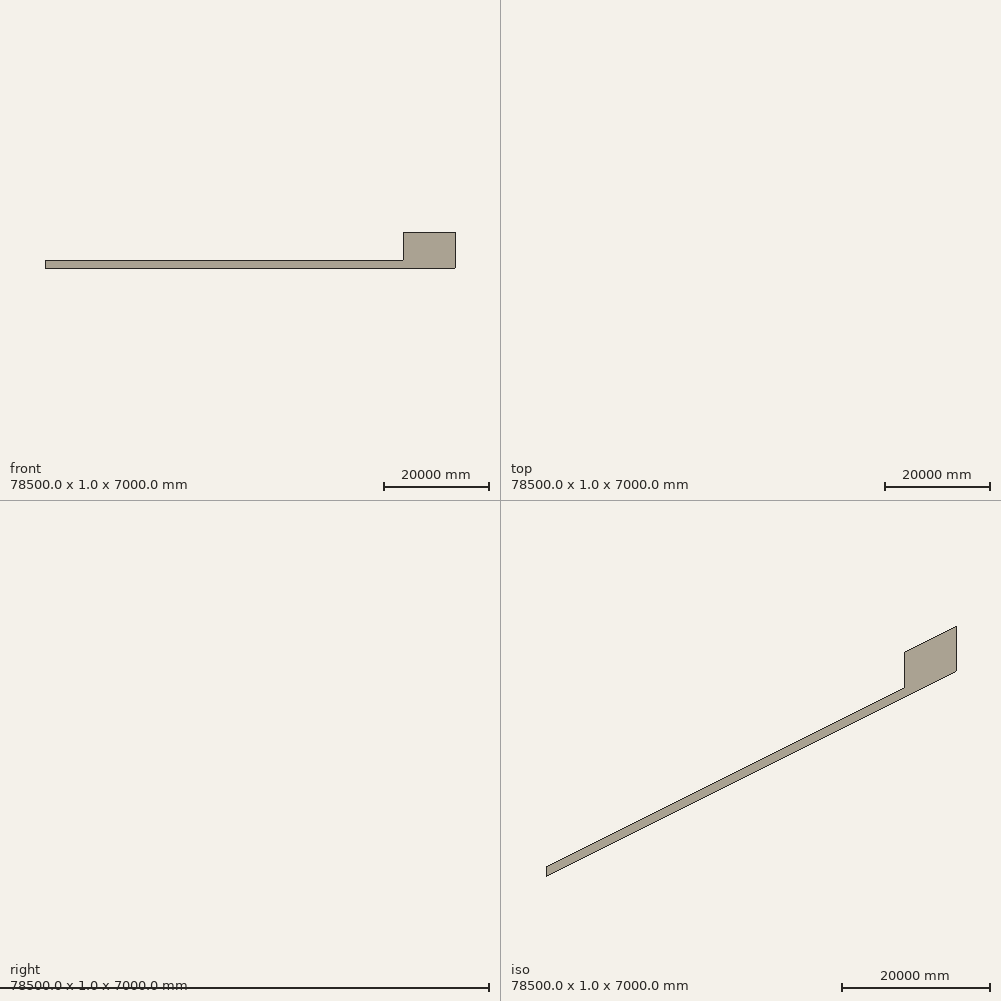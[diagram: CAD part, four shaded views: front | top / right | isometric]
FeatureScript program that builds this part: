
annotation { "Feature Type Name" : "Feature", "Feature Type Description" : "" }
export const myFeature = defineFeature(function(context is Context, id is Id, definition is map)
    precondition{}
    {
        {
            var Q0;
            Q0=qCreatedBy(makeId("Front.planeOp"),FACE);
            var sketch = newSketch(context, id + "F0", { "sketchPlane" : qUnion([Q0])});
            skLineSegment(sketch, "E0", {"start": v(0, -14427.73) * mm, "end": v(63500, -14427.73) * mm});
            skLineSegment(sketch, "E1", {"start": v(63500, -14427.73) * mm, "end": v(63500, -8927.73) * mm});
            skLineSegment(sketch, "E2", {"start": v(63500, -8927.73) * mm, "end": v(73500, -8927.73) * mm});
            skLineSegment(sketch, "E3", {"start": v(73500, -8927.73) * mm, "end": v(73500, -15927.73) * mm});
            skLineSegment(sketch, "E4", {"start": v(73500, -15927.73) * mm, "end": v(1500, -15927.73) * mm});
            skLineSegment(sketch, "E5", {"start": v(1500, -15927.73) * mm, "end": v(1500, -15927.73) * mm});
            skLineSegment(sketch, "E6", {"start": v(0, -14427.73) * mm, "end": v(-5000, -14427.73) * mm});
            skLineSegment(sketch, "E7", {"start": v(-5000, -14427.73) * mm, "end": v(-5000, -15927.73) * mm});
            skLineSegment(sketch, "E8", {"start": v(0, -14427.73) * mm, "end": v(0, -14427.73) * mm});
            skLineSegment(sketch, "E9", {"start": v(1500, -15927.73) * mm, "end": v(-5000, -15927.73) * mm});
            skSolve(sketch);
        }
        {
            var Q0;
            Q0 = qSketchRegion(id + "F0", true);
            extrude(context, id + "F1", {"entities" : qUnion([Q0]), "depth" : 1 * mm, "offsetDistance" : 25 * mm});
        }
    });
